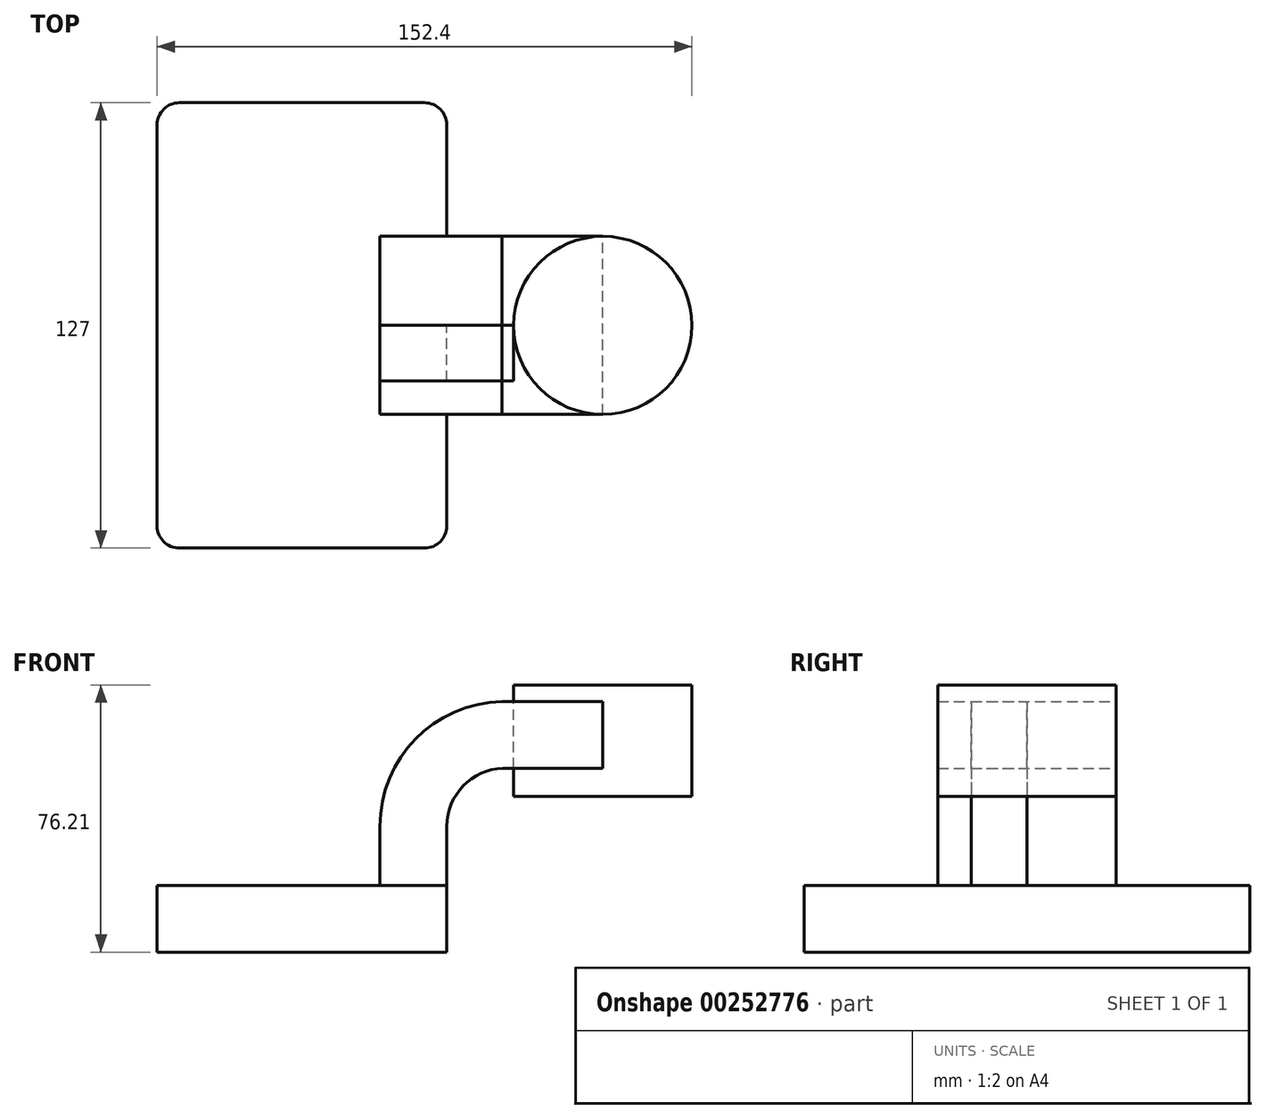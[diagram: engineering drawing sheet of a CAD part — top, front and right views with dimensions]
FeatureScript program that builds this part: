
annotation { "Feature Type Name" : "Feature", "Feature Type Description" : "" }
export const myFeature = defineFeature(function(context is Context, id is Id, definition is map)
    precondition{}
    {
        {
            var Q0;
            Q0=qCreatedBy(makeId("Front.planeOp"),FACE);
            var sketch = newSketch(context, id + "F0", { "sketchPlane" : qUnion([Q0])});
            skLineSegment(sketch, "E0.bottom", {"start": v(41.27, 9.53) * mm, "end": v(-41.28, 9.53) * mm});
            skLineSegment(sketch, "E0.top", {"start": v(41.28, -9.52) * mm, "end": v(-41.27, -9.52) * mm});
            skLineSegment(sketch, "E0.left", {"start": v(41.28, 9.53) * mm, "end": v(41.28, -9.52) * mm});
            skLineSegment(sketch, "E0.right", {"start": v(-41.28, 9.53) * mm, "end": v(-41.27, -9.52) * mm});
            skPoint(sketch, "E0.middle", {"position": v(0, 0) * mm});
            skLineSegment(sketch, "E1", {"start": v(41.27, 9.53) * mm, "end": v(41.27, 26.37) * mm});
            skArc(sketch, "E2", {"start": v(41.27, 26.37) * mm, "mid": v(45.92, 37.86) * mm, "end": v(57.25, 42.88) * mm});
            skLineSegment(sketch, "E3.bottom", {"start": v(111.12, 34.93) * mm, "end": v(60.32, 34.93) * mm});
            skLineSegment(sketch, "E3.top", {"start": v(111.12, 66.68) * mm, "end": v(60.32, 66.68) * mm});
            skLineSegment(sketch, "E3.left", {"start": v(111.12, 34.93) * mm, "end": v(111.12, 66.68) * mm});
            skLineSegment(sketch, "E3.right", {"start": v(60.32, 34.93) * mm, "end": v(60.32, 66.68) * mm});
            skPoint(sketch, "E3.middle", {"position": v(85.72, 50.8) * mm});
            skLineSegment(sketch, "E4", {"start": v(57.25, 42.88) * mm, "end": v(85.72, 42.88) * mm});
            skLineSegment(sketch, "E5.0", {"start": v(57, 61.93) * mm, "end": v(85.72, 61.93) * mm});
            skArc(sketch, "E5.1", {"start": v(22.22, 26.37) * mm, "mid": v(32.36, 51.24) * mm, "end": v(57, 61.93) * mm});
            skLineSegment(sketch, "E5.2", {"start": v(22.22, 9.53) * mm, "end": v(22.22, 26.37) * mm});
            skLineSegment(sketch, "E6", {"start": v(85.72, 66.68) * mm, "end": v(85.72, 34.93) * mm});
            skFitSpline(sketch, "E7", {"points": [v(-41.28, 9.52) * mm, v(57, 61.93) * mm], "startDerivative": vector(98.27, 52.4) * mm, "endDerivative": vector(132.73, 2.89) * mm});
            skSolve(sketch);
        }
        {
            var Q0;
            Q0=qCreatedBy(makeId("Front.planeOp"),FACE);
            var sketch = newSketch(context, id + "F1", { "sketchPlane" : qUnion([Q0])});
            skSolve(sketch);
        }
        {
            var Q0;
            {var subQ0=sQuery(id+"F0.wireOp",EDGE,"E3.left");Q0=makeQuery(id+"F0.imprint","IMPRINT",FACE,{"disambiguationData":[TD([[makeQuery(id+"F0.imprint","IMPRINT",EDGE,{"derivedFrom":subQ0}),1.0]])]});}
            var Q1;
            Q1=sQuery(id+"F0.wireOp",EDGE,"E6");
            revolve(context, id + "F2", {"entities" : qUnion([Q0]), "axis" : qUnion([Q1]), "revolveType" : RevolveType.FULL});
        }
        {
            var Q0;
            Q0 = qSketchRegion(id + "F1", true);
            var Q1;
            Q1=makeQuery(id+"F0.imprint","IMPRINT",FACE,{"disambiguationData":[TD([[makeQuery(id+"F0.imprint","IMPRINT",EDGE,{"derivedFrom":sQuery(id+"F0.wireOp",EDGE,"E5.1")}),1.0]])]});
            extrude(context, id + "F3", {"entities" : qUnion([Q0, Q1]), "depth" : 15.88 * mm});
        }
        {
            var Q0;
            {var subQ7=sQuery(id+"F0.wireOp",EDGE,"E1");Q0=makeQuery(id+"F0.imprint","IMPRINT",FACE,{"disambiguationData":[TD([[makeQuery(id+"F0.imprint","IMPRINT",EDGE,{"derivedFrom":subQ7}),1.0]])]});}
            var Q1;
            {var subQ0=sQuery(id+"F0.wireOp",EDGE,"E4");var subQ1=sQuery(id+"F0.wireOp",EDGE,"E3.right");var subQ2=makeQuery(id+"F0.imprint","INTERSECT",VERTEX,{"derivedFrom":[subQ1,subQ0]});Q1=makeQuery(id+"F0.imprint","IMPRINT",FACE,{"disambiguationData":[TD([[makeQuery(id+"F0.imprint","IMPRINT",EDGE,{"disambiguationData":[TD([[subQ2,-1.0]])],"derivedFrom":subQ1}),-1.0]])]});}
            extrude(context, id + "F4", {"entities" : qUnion([Q0, Q1]), "endBound" : BoundingType.SYMMETRIC, "depth" : 50.8 * mm});
        }
        {
            var Q0;
            Q0=makeQuery(id+"F0.imprint","IMPRINT",FACE,{"disambiguationData":[TD([[makeQuery(id+"F0.imprint","IMPRINT",EDGE,{"derivedFrom":sQuery(id+"F0.wireOp",EDGE,"E0.top")}),-1.0]])]});
            extrude(context, id + "F5", {"entities" : qUnion([Q0]), "endBound" : BoundingType.SYMMETRIC, "oppositeDirection" : true, "depth" : 127 * mm});
        }
        {
            var Q0;
            Q0=makeQuery(id+"F5.opExtrude","CAP_EDGE",EDGE,{"disambiguationData":[OSD([sQuery(id+"F0.wireOp",EDGE,"E0.left")])],"isStart":true});
            var Q1;
            Q1=makeQuery(id+"F5.opExtrude","CAP_EDGE",EDGE,{"disambiguationData":[OSD([sQuery(id+"F0.wireOp",EDGE,"E0.right")])],"isStart":true});
            var Q2;
            Q2=makeQuery(id+"F5.opExtrude","CAP_EDGE",EDGE,{"disambiguationData":[OSD([sQuery(id+"F0.wireOp",EDGE,"E0.left")])],"isStart":false});
            var Q3;
            Q3=makeQuery(id+"F5.opExtrude","CAP_EDGE",EDGE,{"disambiguationData":[OSD([sQuery(id+"F0.wireOp",EDGE,"E0.right")])],"isStart":false});
            fillet(context, id + "F6", {"entities" : qUnion([Q0, Q1, Q2, Q3]), "radius" : 6.35 * mm, "tangentPropagation" : true, "allowEdgeOverflow" : false});
        }
    });
